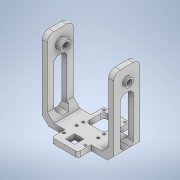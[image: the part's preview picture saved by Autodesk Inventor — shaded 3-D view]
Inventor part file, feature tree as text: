
AUTODESK INVENTOR PART (.ipt)
format: ipt  version: 2020 (Build 240168000, 168)  size: 309,248 bytes
history: native  units: in
note: dims shown in document units (in); Inventor stores cm internally (conversion verified against a paired STEP export)
features: extrude x10, sketch x10, fillet x3, chamfer x2
ambient origin geometry x8: Origin, YZ Plane, XZ Plane, XY Plane, X Axis, Y Axis, Z Axis, Center Point
bodies: Solid1 (feature_tree)
feature tree (25):
  extrude  "Extrusion1"  Depth=0.2in
  extrude  "Extrusion2"  Depth=3.0in
  extrude  "Extrusion3"  Depth=2.0in
  extrude  "Extrusion4"  Depth=1.0in TaperAngle=0.0deg
  extrude  "Extrusion5"  Depth=0.9843in
  extrude  "Extrusion6"  Depth=0.0787in
  fillet  "Fillet1"  Radius=0.0787in
  fillet  "Fillet2"  Radius=0.0787in
  chamfer  "Chamfer1"  Distance=1.0in
  extrude  "Extrusion7"  Depth=0.1in
  chamfer  "Chamfer2"  Distance=0.8in
  fillet  "Fillet3"  Radius=0.7in
  extrude  "Extrusion8"  Depth=1.0in TaperAngle=0.0deg
  extrude  "Extrusion9"  Depth=1.0in
  extrude  "Extrusion10"  Depth=0.25in
  sketch  "Sketch1"  dims[d0=2.75in d1=0.2in]
  sketch  "Sketch2"  dims[d2=0.2in d3=3.0in]
  sketch  "Sketch3"  dims[d4=1.0in d5=0.0in d6=2.0in]
  sketch  "Sketch4"  dims[d7=1.0in d8=1.0in d9=0.0in]
  sketch  "Sketch5"  dims[d10=0.9394in d11=0.9843in]
  sketch  "Sketch6"  dims[d12=0.0984in d13=0.0787in d14=0.0787in d15=0.0787in]
  sketch  "Sketch7"  dims[d16=0.5709in]
  sketch  "Sketch8"  dims[d17=0.3543in]
  sketch  "Sketch9"  dims[d18=0.3725in]
  sketch  "Sketch10"  dims[d19=0.4921in d20=1.0in d21=0.0in d22=0.0984in d23=0.8in d24=0.7in d25=1.0in d26=0.0in d27=1.0in d28=0.25in d29=0.2283in d31=1.0in d32=0.0in d35=1.0in d36=0.0in d37=0.0787in d38=0.25in d39=0.25in d40=0.125in d41=45.0deg d42=0.25in d43=0.0in d44=0.25in d46=0.25in d47=0.0in d48=0.0in d49=0.125in d50=0.125in d51=45.0deg d52=1.0in d53=0.205in d54=0.0079in d55=0.125in d56=0.063in d57=0.1781in d58=0.0in d59=0.063in d60=0.2126in d61=0.0in d62=0.063in d63=0.1in d64=0.0in]
